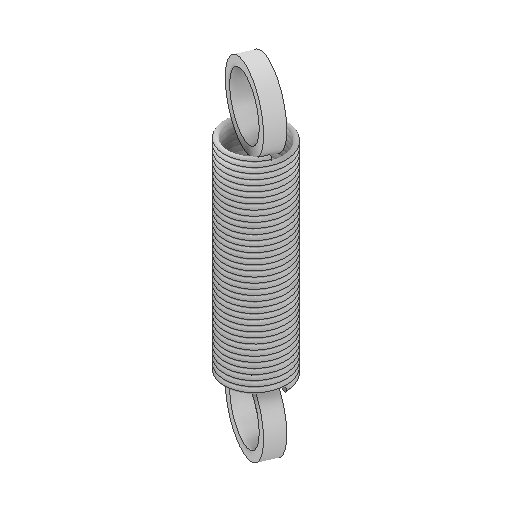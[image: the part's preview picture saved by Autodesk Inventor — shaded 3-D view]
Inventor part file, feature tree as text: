
AUTODESK INVENTOR PART (.ipt)
format: ipt  version: 2025 (Build 290162010, 162A)  size: 605,184 bytes
history: native  units: in
note: dims shown in document units (in); Inventor stores cm internally (conversion verified against a paired STEP export)
features: sketch x3, helix x1, extrude x1
ambient origin geometry x8: Origin, YZ Plane, XZ Plane, XY Plane, X Axis, Y Axis, Z Axis, Center Point
bodies: Solid1 (feature_tree)
feature tree (5):
  helix  "Coil1"  [1 undecoded]
  sketch  "Sketch2"  dims[d3=0.03in d4=1.168in]
  extrude  "Extrusion1"  Depth=0.163in
  sketch  "Sketch1"  dims[d1=0.025in d2=0.163in]
  sketch  "Sketch3"  dims[d5=1.9685in d6=0.0in d7=90.0deg d8=90.0deg d9=0.0in d10=0.0in d11=0.33in d12=0.33in d13=1.5in d14=0.05in d15=0.05in d16=0.1in d17=0.0in]
note: 1 required parameter value undecoded (feature->parameter linkage not recoverable at this tier; creation-order binding heuristic only, values carry confidence <= 0.55)
